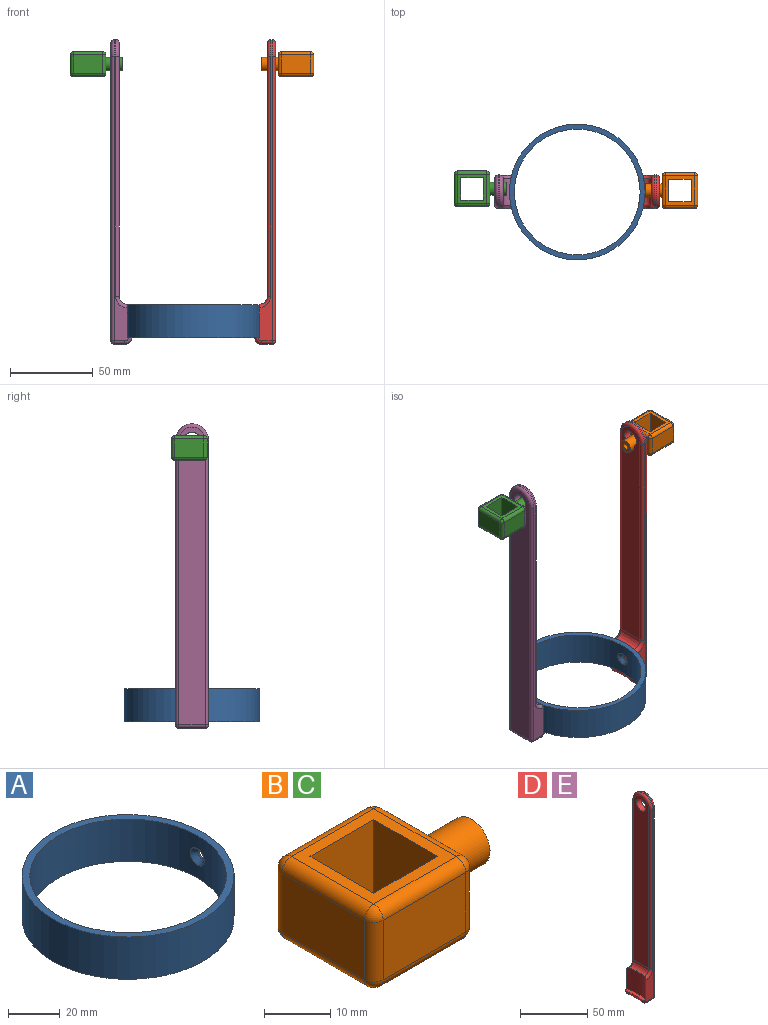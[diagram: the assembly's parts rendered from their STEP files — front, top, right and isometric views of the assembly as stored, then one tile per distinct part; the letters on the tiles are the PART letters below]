
ASSEMBLY  parts=5 mates=6
PART A: 8 faces, bbox 82x82x20 mm
  f0: cylinder r=38mm len=76mm, axis (0,0,-1), area 4727.4mm2, adj f2,f3,f4,f7
  f1: cylinder r=41mm len=82mm, axis (0,0,-1), area 5140.2mm2, adj f2,f3,f5
  f2: plane 82x82mm, normal (0,0,1), area 744.6mm2, adj f0,f1
  f3: plane 82x82mm, normal (0,0,-1), area 744.6mm2, adj f0,f1
  f4: cylinder r=3.9mm len=7.8mm, axis (-1,0,0), area 1.2mm2, adj f0,f6
  f5: cylinder r=1.96mm len=3.91mm, axis (-1,0,0), area 9.1mm2, adj f1,f6
  f6: cone r=1.96mm half-angle=41deg, axis (-1,0,0), area 54.5mm2, adj f4,f5,f7
  f7: cylinder r=3.9mm len=7.8mm, axis (-1,0,0), area 1.2mm2, adj f0,f6
PART B: 34 faces, bbox 31.6x21.6x15 mm
  f0: plane 15x13.6mm, normal (0,1,0), area 204mm2, adj f1,f7,f8,f9
  f1: plane 15x13.6mm, normal (1,0,0), area 204mm2, adj f0,f2,f8,f9
  f2: plane 15x13.6mm, normal (0,-1,0), area 204mm2, adj f1,f7,f8,f9
  f3: plane 17.6x11mm, normal (0,1,0), area 193.6mm2, adj f22,f27,f30,f33
  f4: plane 17.6x11mm, normal (-1,0,0), area 193.6mm2, adj f19,f28,f29,f33
  f5: plane 17.6x11mm, normal (0,-1,0), area 193.6mm2, adj f14,f18,f19,f20
  f6: plane 17.6x11mm, normal (1,0,0), area 143.3mm2, adj f10,f14,f17,f21,f22
  f7: plane 15x13.6mm, normal (-1,0,0), area 204mm2, adj f0,f2,f8,f9
  f8: plane 17.6x17.6mm, normal (0,0,1), area 124.8mm2, adj f0,f1,f2,f7,f17,f18,f27,f28
  f9: plane 17.6x17.6mm, normal (0,0,-1), area 124.8mm2, adj f0,f1,f2,f7,f20,f21,f29,f30
  f10: cylinder r=4mm len=10mm, axis (-1,0,0), area 251.3mm2, adj f6,f11
  f11: plane 8x8mm, normal (1,0,0), area 38.2mm2, adj f10,f13
  f12: cone r=0mm half-angle=59deg, axis (1,0,0), area 14mm2, adj f13
  f13: cylinder r=1.96mm len=10mm, axis (1,0,0), area 122.9mm2, adj f11,f12
  f14: cylinder r=2mm len=11mm, axis (0,0,-1), area 34.6mm2, adj f5,f6,f15,f16
  f15: sphere r=2mm, area 6.3mm2, adj f14,f17,f18
  f16: sphere r=2mm, area 6.3mm2, adj f14,f20,f21
  f17: cylinder r=2mm len=17.6mm, axis (0,-1,0), area 55.3mm2, adj f6,f8,f15,f23
  f18: cylinder r=2mm len=17.6mm, axis (-1,0,0), area 55.3mm2, adj f5,f8,f15,f24
  f19: cylinder r=2mm len=11mm, axis (0,0,1), area 34.6mm2, adj f4,f5,f24,f25
  f20: cylinder r=2mm len=17.6mm, axis (1,0,0), area 55.3mm2, adj f5,f9,f16,f25
  f21: cylinder r=2mm len=17.6mm, axis (0,1,0), area 55.3mm2, adj f6,f9,f16,f26
  f22: cylinder r=2mm len=11mm, axis (0,0,1), area 34.6mm2, adj f3,f6,f23,f26
  f23: sphere r=2mm, area 6.3mm2, adj f17,f22,f27
  f24: sphere r=2mm, area 6.3mm2, adj f18,f19,f28
  f25: sphere r=2mm, area 6.3mm2, adj f19,f20,f29
  f26: sphere r=2mm, area 6.3mm2, adj f21,f22,f30
  f27: cylinder r=2mm len=17.6mm, axis (1,0,0), area 55.3mm2, adj f3,f8,f23,f31
  f28: cylinder r=2mm len=17.6mm, axis (0,1,0), area 55.3mm2, adj f4,f8,f24,f31
  f29: cylinder r=2mm len=17.6mm, axis (0,-1,0), area 55.3mm2, adj f4,f9,f25,f32
  f30: cylinder r=2mm len=17.6mm, axis (-1,0,0), area 55.3mm2, adj f3,f9,f26,f32
  f31: sphere r=2mm, area 6.3mm2, adj f27,f28,f33
  f32: sphere r=2mm, area 6.3mm2, adj f29,f30,f33
  f33: cylinder r=2mm len=11mm, axis (0,0,-1), area 34.6mm2, adj f3,f4,f31,f32
PART C: same geometry as B
PART D: 26 faces, bbox 13.1x21.7x184.9 mm
  f0: cylinder r=41mm len=20mm, axis (0,0,-1), area 399.9mm2, adj f2,f3,f5,f8,f10,f14
  f1: plane 180x16mm, normal (1,0,0), area 2774mm2, adj f19,f21,f22,f24,f25
  f2: plane 172x8.57mm, normal (0,1,0), area 322.6mm2, adj f0,f5,f7,f10,f11,f17,f20,f24
  f3: plane 172x8.57mm, normal (0,-1,0), area 322.6mm2, adj f0,f5,f7,f13,f14,f15,f16,f19
  f4: plane 16x6.53mm, normal (0,0,-1), area 96.3mm2, adj f9,f16,f20,f21
  f5: plane 20.09x3.9mm, normal (0,0,1), area 57.8mm2, adj f0,f2,f3,f9,f15,f17
  f6: plane 153.16x16mm, normal (-1,0,0), area 2343.6mm2, adj f8,f11,f12,f13,f25
  f7: cylinder r=10mm len=20mm, axis (1,0,0), area 31.4mm2, adj f2,f3,f12,f22
  f8: bspline ~19.61x5.19mm, area 109.8mm2, adj f0,f6,f10,f14
  f9: torus R=42mm, axis (0,0,1), area 97.4mm2, adj f4,f5,f15,f17
  f10: bspline ~8.21x7.99mm, area 27.7mm2, adj f0,f2,f8,f11
  f11: cylinder r=2mm len=145.02mm, axis (0,0,1), area 455.6mm2, adj f2,f6,f10,f12
  f12: torus R=8mm, axis (1,0,0), area 91.5mm2, adj f6,f7,f11,f13
  f13: cylinder r=2mm len=145.02mm, axis (0,0,-1), area 455.6mm2, adj f3,f6,f12,f14
  f14: bspline ~8.21x7.99mm, area 27.7mm2, adj f0,f3,f8,f13
  f15: bspline ~4.87x4.64mm, area 17.8mm2, adj f3,f5,f9,f16
  f16: cylinder r=2mm len=6.53mm, axis (1,0,0), area 20.5mm2, adj f3,f4,f15,f18
  f17: bspline ~4.87x4.64mm, area 17.8mm2, adj f2,f5,f9,f20
  f18: sphere r=2mm, area 6.3mm2, adj f16,f19,f21
  f19: cylinder r=2mm len=172mm, axis (0,0,1), area 540.4mm2, adj f1,f3,f18,f22
  f20: cylinder r=2mm len=6.53mm, axis (-1,0,0), area 20.5mm2, adj f2,f4,f17,f23
  f21: cylinder r=2mm len=16mm, axis (0,1,0), area 50.3mm2, adj f1,f4,f18,f23
  f22: torus R=8mm, axis (1,0,0), area 91.5mm2, adj f1,f7,f19,f24
  f23: sphere r=2mm, area 4mm2, adj f20,f21,f24
  f24: cylinder r=2mm len=172mm, axis (0,0,-1), area 540.4mm2, adj f1,f2,f22,f23
  f25: cylinder r=5mm len=10mm, axis (-1,0,0), area 157.1mm2, adj f1,f6
PART E: same geometry as D
PLACE A t=(67.44,-33.95,-183.78)mm
PLACE B rot(axis=(0,0,-1),180deg) t=(136.3,-26.54,-25.97)mm
PLACE C t=(-2.9,-39.14,-25.97)mm
PLACE D t=(67.44,-33.95,-183.78)mm
PLACE E rot(axis=(0,0,-1),180deg) t=(67.44,-33.95,-183.78)mm
MATE parallel B.f3 <-> C.f5  axis (0,-1,0) through (129.5,-44.14,-18.47)mm
MATE parallel D.f0 <-> A.f1  axis (0,0,-1) through (67.44,-33.95,-173.78)mm
MATE parallel B.f10 <-> C.f10  axis (1,0,0) through (122.7,-33.34,-18.47)mm
MATE planar D.f0 <-> A.f1  axis (0,0,-1) through (67.44,-33.95,-173.78)mm
MATE planar A.f1 <-> E.f0  axis (0,0,-1) through (67.44,-33.95,-173.78)mm
MATE parallel E.f0 <-> A.f1  axis (0,0,-1) through (67.44,-33.95,-173.78)mm
